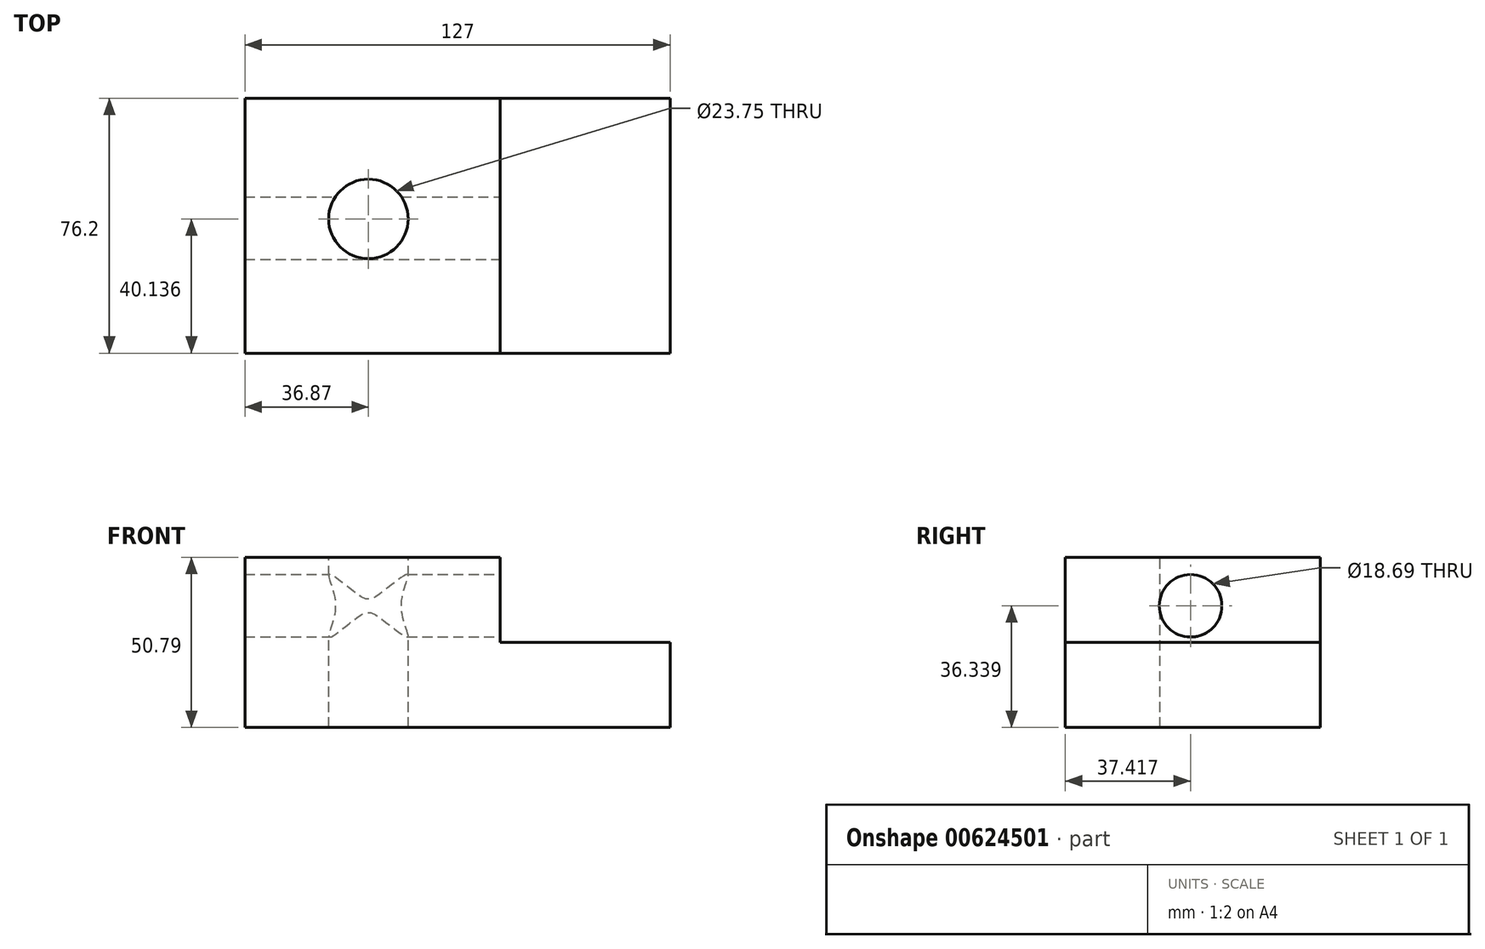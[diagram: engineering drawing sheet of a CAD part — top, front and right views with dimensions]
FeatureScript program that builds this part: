
annotation { "Feature Type Name" : "Feature", "Feature Type Description" : "" }
export const myFeature = defineFeature(function(context is Context, id is Id, definition is map)
    precondition{}
    {
        {
            var Q0;
            Q0=qCreatedBy(makeId("Front.planeOp"),FACE);
            var sketch = newSketch(context, id + "F0", { "sketchPlane" : qUnion([Q0])});
            skLineSegment(sketch, "E0.bottom", {"start": v(0, 0) * mm, "end": v(127, 0) * mm});
            skLineSegment(sketch, "E0.top", {"start": v(0, 50.79) * mm, "end": v(127, 50.79) * mm});
            skLineSegment(sketch, "E0.left", {"start": v(0, 0) * mm, "end": v(0, 50.79) * mm});
            skLineSegment(sketch, "E0.right", {"start": v(127, 0) * mm, "end": v(127, 50.79) * mm});
            skLineSegment(sketch, "E1.bottom", {"start": v(127, 50.79) * mm, "end": v(76.2, 50.79) * mm});
            skLineSegment(sketch, "E1.top", {"start": v(127, 25.39) * mm, "end": v(76.2, 25.39) * mm});
            skLineSegment(sketch, "E1.left", {"start": v(127, 50.79) * mm, "end": v(127, 25.39) * mm});
            skLineSegment(sketch, "E1.right", {"start": v(76.2, 50.79) * mm, "end": v(76.2, 25.39) * mm});
            skSolve(sketch);
        }
        {
            var Q0;
            Q0=makeQuery(id+"F0.imprint","IMPRINT",FACE,{"disambiguationData":[TD([[makeQuery(id+"F0.imprint","IMPRINT",EDGE,{"derivedFrom":sQuery(id+"F0.wireOp",EDGE,"E0.bottom")}),1.0]])]});
            extrude(context, id + "F1", {"entities" : qUnion([Q0]), "depth" : 76.2 * mm, "offsetDistance" : 25.4 * mm});
        }
        {
            var Q0;
            Q0=makeQuery(id+"F1.opExtrude","SWEPT_FACE",FACE,{"disambiguationData":[OSD([sQuery(id+"F0.wireOp",EDGE,"E0.top")])]});
            var sketch = newSketch(context, id + "F2", { "sketchPlane" : qUnion([Q0])});
            skCircle(sketch, "E2", {"center": v(36.87, -36.06) * mm, "radius": 11.88 * mm});
            skSolve(sketch);
        }
        {
            var Q0;
            Q0=sQuery(id+"F2.wireOp",VERTEX,"E2.center");
            var Q1;
            Q1=makeQuery(id+"F1.opExtrude","SWEPT_BODY",BODY,{"disambiguationData":[OSD([sQuery(id+"F0.wireOp",EDGE,"E0.bottom"),sQuery(id+"F0.wireOp",EDGE,"E0.top"),sQuery(id+"F0.wireOp",EDGE,"E0.left"),sQuery(id+"F0.wireOp",EDGE,"E0.right"),sQuery(id+"F0.wireOp",EDGE,"E1.top"),sQuery(id+"F0.wireOp",EDGE,"E1.right")])]});
            hole(context, id + "F3", {"style" : HoleStyle.SIMPLE, "endStyle" : HoleEndStyle.THROUGH, "holeDiameter" : 23.75 * mm, "majorDiameter" : 6.35 * mm, "isTappedThrough" : true, "tappedDepth" : 12.7 * mm, "tapClearance" : 3, "locations" : qUnion([Q0]), "scope" : qUnion([Q1])});
        }
        {
            var Q0;
            Q0=makeQuery(id+"F1.opExtrude","SWEPT_FACE",FACE,{"disambiguationData":[OSD([sQuery(id+"F0.wireOp",EDGE,"E1.right")])]});
            var sketch = newSketch(context, id + "F4", { "sketchPlane" : qUnion([Q0])});
            skCircle(sketch, "E3", {"center": v(-38.78, 36.34) * mm, "radius": 9.7 * mm});
            skSolve(sketch);
        }
        {
            var Q0;
            Q0=sQuery(id+"F4.wireOp",VERTEX,"E3.center");
            var Q1;
            Q1=makeQuery(id+"F1.opExtrude","SWEPT_BODY",BODY,{"disambiguationData":[OSD([sQuery(id+"F0.wireOp",EDGE,"E0.bottom"),sQuery(id+"F0.wireOp",EDGE,"E0.top"),sQuery(id+"F0.wireOp",EDGE,"E0.left"),sQuery(id+"F0.wireOp",EDGE,"E0.right"),sQuery(id+"F0.wireOp",EDGE,"E1.top"),sQuery(id+"F0.wireOp",EDGE,"E1.right")])]});
            hole(context, id + "F5", {"style" : HoleStyle.SIMPLE, "endStyle" : HoleEndStyle.THROUGH, "holeDiameter" : 18.7 * mm, "majorDiameter" : 6.35 * mm, "isTappedThrough" : true, "tappedDepth" : 12.7 * mm, "tapClearance" : 3, "locations" : qUnion([Q0]), "scope" : qUnion([Q1])});
        }
    });
